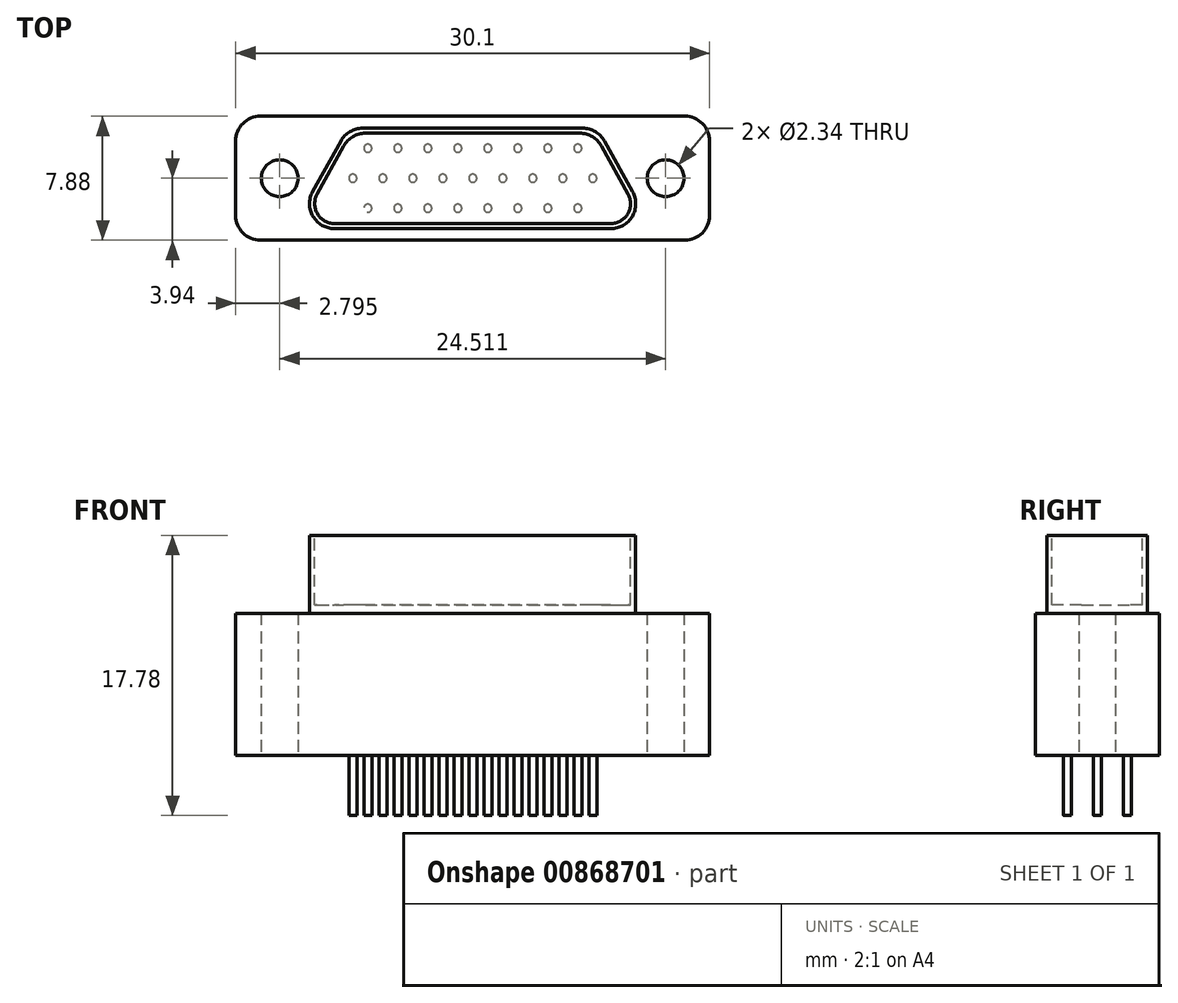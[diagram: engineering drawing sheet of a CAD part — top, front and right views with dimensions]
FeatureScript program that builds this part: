
annotation { "Feature Type Name" : "Feature", "Feature Type Description" : "" }
export const myFeature = defineFeature(function(context is Context, id is Id, definition is map)
    precondition{}
    {
        {
            var Q0;
            Q0=qCreatedBy(makeId("Top.planeOp"),FACE);
            var sketch = newSketch(context, id + "F0", { "sketchPlane" : qUnion([Q0])});
            skLineSegment(sketch, "E0.bottom", {"start": v(-13.47, 3.94) * mm, "end": v(13.47, 3.94) * mm});
            skLineSegment(sketch, "E0.top", {"start": v(-13.47, -3.94) * mm, "end": v(13.47, -3.94) * mm});
            skLineSegment(sketch, "E0.left", {"start": v(-15.05, 2.36) * mm, "end": v(-15.05, -2.36) * mm});
            skLineSegment(sketch, "E0.right", {"start": v(15.05, 2.36) * mm, "end": v(15.05, -2.36) * mm});
            skPoint(sketch, "E0.middle", {"position": v(0, 0) * mm});
            skCircle(sketch, "E1", {"center": v(-12.26, 0) * mm, "radius": 1.17 * mm});
            skCircle(sketch, "E2", {"center": v(12.26, 0) * mm, "radius": 1.17 * mm});
            skPoint(sketch, "E3.visualSharp", {"position": v(-15.05, -3.94) * mm});
            skArc(sketch, "E3.filletArc", {"start": v(-15.05, -2.36) * mm, "mid": v(-14.59, -3.48) * mm, "end": v(-13.47, -3.94) * mm});
            skPoint(sketch, "E4.visualSharp", {"position": v(-15.05, 3.94) * mm});
            skArc(sketch, "E4.filletArc", {"start": v(-13.47, 3.94) * mm, "mid": v(-14.59, 3.48) * mm, "end": v(-15.05, 2.36) * mm});
            skPoint(sketch, "E5.visualSharp", {"position": v(15.05, 3.94) * mm});
            skArc(sketch, "E5.filletArc", {"start": v(15.05, 2.36) * mm, "mid": v(14.59, 3.48) * mm, "end": v(13.47, 3.94) * mm});
            skPoint(sketch, "E6.visualSharp", {"position": v(15.05, -3.94) * mm});
            skArc(sketch, "E6.filletArc", {"start": v(13.47, -3.94) * mm, "mid": v(14.59, -3.48) * mm, "end": v(15.05, -2.36) * mm});
            skSolve(sketch);
        }
        {
            var Q0;
            Q0=makeQuery(id+"F0.imprint","IMPRINT",FACE,{"disambiguationData":[TD([[makeQuery(id+"F0.imprint","IMPRINT",EDGE,{"derivedFrom":sQuery(id+"F0.wireOp",EDGE,"E0.bottom")}),-1.0]])]});
            extrude(context, id + "F1", {"entities" : qUnion([Q0]), "endBound" : BoundingType.SYMMETRIC, "depth" : 9.02 * mm, "offsetDistance" : 25.4 * mm});
        }
        {
            var Q0;
            Q0=makeQuery(id+"F1.opExtrude","CAP_FACE",FACE,{"disambiguationData":[OSD([sQuery(id+"F0.wireOp",EDGE,"E0.bottom"),sQuery(id+"F0.wireOp",EDGE,"E0.top"),sQuery(id+"F0.wireOp",EDGE,"E0.left"),sQuery(id+"F0.wireOp",EDGE,"E0.right"),sQuery(id+"F0.wireOp",EDGE,"E1"),sQuery(id+"F0.wireOp",EDGE,"E2"),sQuery(id+"F0.wireOp",EDGE,"E3.filletArc"),sQuery(id+"F0.wireOp",EDGE,"E4.filletArc"),sQuery(id+"F0.wireOp",EDGE,"E5.filletArc"),sQuery(id+"F0.wireOp",EDGE,"E6.filletArc")])],"isStart":false});
            var sketch = newSketch(context, id + "F2", { "sketchPlane" : qUnion([Q0])});
            skPoint(sketch, "E7.middle", {"position": v(0, 0) * mm});
            skLineSegment(sketch, "E8.top", {"start": v(8.78, -3.2) * mm, "end": v(-8.78, -3.2) * mm});
            skLineSegment(sketch, "E9", {"start": v(-7, 3.17) * mm, "end": v(7, 3.18) * mm});
            skLineSegment(sketch, "E10", {"start": v(-10.16, -0.86) * mm, "end": v(-8.37, 2.36) * mm});
            skLineSegment(sketch, "E11", {"start": v(8.37, 2.36) * mm, "end": v(10.16, -0.86) * mm});
            skPoint(sketch, "E12.visualSharp", {"position": v(-7.92, 3.17) * mm});
            skArc(sketch, "E12.filletArc", {"start": v(-7, 3.17) * mm, "mid": v(-7.8, 2.96) * mm, "end": v(-8.37, 2.36) * mm});
            skPoint(sketch, "E13.visualSharp", {"position": v(-11.46, -3.2) * mm});
            skArc(sketch, "E13.filletArc", {"start": v(-10.16, -0.86) * mm, "mid": v(-10.14, -2.42) * mm, "end": v(-8.78, -3.2) * mm});
            skPoint(sketch, "E14.visualSharp", {"position": v(11.46, -3.2) * mm});
            skArc(sketch, "E14.filletArc", {"start": v(8.78, -3.2) * mm, "mid": v(10.14, -2.42) * mm, "end": v(10.16, -0.86) * mm});
            skPoint(sketch, "E15.visualSharp", {"position": v(7.92, 3.18) * mm});
            skArc(sketch, "E15.filletArc", {"start": v(8.37, 2.36) * mm, "mid": v(7.8, 2.96) * mm, "end": v(7, 3.18) * mm});
            skSolve(sketch);
        }
        {
            var Q0;
            Q0=qSketchRegion(id+"F2",true);
            extrude(context, id + "F3", {"entities" : qUnion([Q0]), "operationType" : NewBodyOperationType.ADD, "depth" : 4.95 * mm, "offsetDistance" : 25.4 * mm});
        }
        {
            var Q0;
            Q0=makeQuery(id+"F3.opExtrude","CAP_FACE",FACE,{"disambiguationData":[OSD([sQuery(id+"F2.wireOp",EDGE,"E8.top"),sQuery(id+"F2.wireOp",EDGE,"E9"),sQuery(id+"F2.wireOp",EDGE,"E10"),sQuery(id+"F2.wireOp",EDGE,"E11"),sQuery(id+"F2.wireOp",EDGE,"E12.filletArc"),sQuery(id+"F2.wireOp",EDGE,"E13.filletArc"),sQuery(id+"F2.wireOp",EDGE,"E14.filletArc"),sQuery(id+"F2.wireOp",EDGE,"E15.filletArc")])],"isStart":false});
            var sketch = newSketch(context, id + "F4", { "sketchPlane" : qUnion([Q0])});
            skLineSegment(sketch, "E16", {"start": v(-6.8, 2.86) * mm, "end": v(6.8, 2.86) * mm});
            skLineSegment(sketch, "E17", {"start": v(8.19, 2.05) * mm, "end": v(9.87, -1) * mm});
            skLineSegment(sketch, "E18", {"start": v(8.76, -2.88) * mm, "end": v(-8.76, -2.88) * mm});
            skLineSegment(sketch, "E19", {"start": v(-9.87, -1) * mm, "end": v(-8.18, 2.05) * mm});
            skPoint(sketch, "E20.visualSharp", {"position": v(-10.92, -2.88) * mm});
            skArc(sketch, "E20.filletArc", {"start": v(-9.87, -1) * mm, "mid": v(-9.85, -2.26) * mm, "end": v(-8.76, -2.88) * mm});
            skPoint(sketch, "E21.visualSharp", {"position": v(-7.73, 2.86) * mm});
            skArc(sketch, "E21.filletArc", {"start": v(-6.8, 2.86) * mm, "mid": v(-7.6, 2.64) * mm, "end": v(-8.18, 2.05) * mm});
            skPoint(sketch, "E22.visualSharp", {"position": v(7.74, 2.86) * mm});
            skArc(sketch, "E22.filletArc", {"start": v(8.19, 2.05) * mm, "mid": v(7.6, 2.64) * mm, "end": v(6.8, 2.86) * mm});
            skPoint(sketch, "E23.visualSharp", {"position": v(10.92, -2.88) * mm});
            skArc(sketch, "E23.filletArc", {"start": v(8.76, -2.88) * mm, "mid": v(9.86, -2.26) * mm, "end": v(9.87, -1) * mm});
            skSolve(sketch);
        }
        {
            var Q0;
            Q0=qSketchRegion(id+"F4",true);
            extrude(context, id + "F5", {"entities" : qUnion([Q0]), "operationType" : NewBodyOperationType.REMOVE, "depth" : -4.4 * mm, "offsetDistance" : 25.4 * mm});
        }
        {
            var Q0;
            Q0=makeQuery(id+"F1.opExtrude","CAP_FACE",FACE,{"disambiguationData":[OSD([sQuery(id+"F0.wireOp",EDGE,"E0.bottom"),sQuery(id+"F0.wireOp",EDGE,"E0.top"),sQuery(id+"F0.wireOp",EDGE,"E0.left"),sQuery(id+"F0.wireOp",EDGE,"E0.right"),sQuery(id+"F0.wireOp",EDGE,"E1"),sQuery(id+"F0.wireOp",EDGE,"E2"),sQuery(id+"F0.wireOp",EDGE,"E3.filletArc"),sQuery(id+"F0.wireOp",EDGE,"E4.filletArc"),sQuery(id+"F0.wireOp",EDGE,"E5.filletArc"),sQuery(id+"F0.wireOp",EDGE,"E6.filletArc")])],"isStart":true});
            var sketch = newSketch(context, id + "F6", { "sketchPlane" : qUnion([Q0])});
            skCircle(sketch, "E24", {"center": v(-6.65, 1.9) * mm, "radius": 0.25 * mm});
            skCircle(sketch, "E25.1.0.0", {"center": v(-4.75, 1.9) * mm, "radius": 0.25 * mm});
            skCircle(sketch, "E25.2.0.0", {"center": v(-2.84, 1.9) * mm, "radius": 0.25 * mm});
            skCircle(sketch, "E25.3.0.0", {"center": v(-0.94, 1.9) * mm, "radius": 0.25 * mm});
            skCircle(sketch, "E25.4.0.0", {"center": v(0.97, 1.9) * mm, "radius": 0.25 * mm});
            skCircle(sketch, "E25.5.0.0", {"center": v(2.87, 1.9) * mm, "radius": 0.25 * mm});
            skCircle(sketch, "E25.6.0.0", {"center": v(4.78, 1.9) * mm, "radius": 0.25 * mm});
            skCircle(sketch, "E25.7.0.0", {"center": v(6.68, 1.9) * mm, "radius": 0.25 * mm});
            skLineSegment(sketch, "E25.direction1", {"start": v(-6.65, 1.9) * mm, "end": v(-4.75, 1.9) * mm, "construction": true});
            skCircle(sketch, "E26", {"center": v(-7.6, 0) * mm, "radius": 0.25 * mm});
            skCircle(sketch, "E27.1.0.0", {"center": v(-5.7, 0) * mm, "radius": 0.25 * mm});
            skCircle(sketch, "E27.2.0.0", {"center": v(-3.8, 0) * mm, "radius": 0.25 * mm});
            skCircle(sketch, "E27.3.0.0", {"center": v(-1.9, 0) * mm, "radius": 0.25 * mm});
            skCircle(sketch, "E27.4.0.0", {"center": v(0.01, 0) * mm, "radius": 0.25 * mm});
            skCircle(sketch, "E27.5.0.0", {"center": v(1.92, 0) * mm, "radius": 0.25 * mm});
            skLineSegment(sketch, "E27.direction1", {"start": v(-7.6, 0) * mm, "end": v(-5.7, 0) * mm, "construction": true});
            skCircle(sketch, "E28", {"center": v(-6.65, -1.9) * mm, "radius": 0.25 * mm});
            skCircle(sketch, "E29.1.0.0", {"center": v(-4.75, -1.9) * mm, "radius": 0.25 * mm});
            skCircle(sketch, "E29.2.0.0", {"center": v(-2.84, -1.9) * mm, "radius": 0.25 * mm});
            skCircle(sketch, "E29.3.0.0", {"center": v(-0.94, -1.9) * mm, "radius": 0.25 * mm});
            skCircle(sketch, "E29.4.0.0", {"center": v(0.97, -1.9) * mm, "radius": 0.25 * mm});
            skCircle(sketch, "E29.5.0.0", {"center": v(2.87, -1.9) * mm, "radius": 0.25 * mm});
            skLineSegment(sketch, "E29.direction1", {"start": v(-6.65, -1.9) * mm, "end": v(-4.75, -1.9) * mm, "construction": true});
            skCircle(sketch, "E30.0.6.0", {"center": v(3.82, 0) * mm, "radius": 0.25 * mm});
            skCircle(sketch, "E30.0.7.0", {"center": v(5.73, 0) * mm, "radius": 0.25 * mm});
            skCircle(sketch, "E30.0.8.0", {"center": v(7.63, 0) * mm, "radius": 0.25 * mm});
            skCircle(sketch, "E31.0.6.0", {"center": v(4.78, -1.9) * mm, "radius": 0.25 * mm});
            skCircle(sketch, "E31.0.7.0", {"center": v(6.68, -1.9) * mm, "radius": 0.25 * mm});
            skSolve(sketch);
        }
        {
            var Q0;
            Q0=qSketchRegion(id+"F6",true);
            extrude(context, id + "F7", {"entities" : qUnion([Q0]), "operationType" : NewBodyOperationType.ADD, "depth" : 3.8 * mm, "offsetDistance" : 25.4 * mm});
        }
    });
